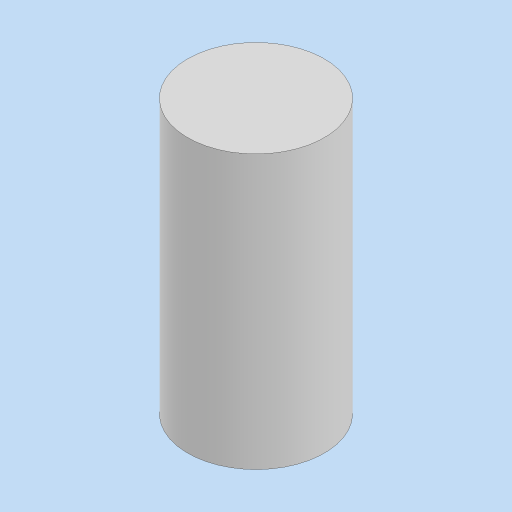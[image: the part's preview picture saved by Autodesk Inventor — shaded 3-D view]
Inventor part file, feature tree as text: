
AUTODESK INVENTOR PART (.ipt)
format: ipt  version: 2024 (Build 280153000, 153)  size: 78,848 bytes
history: native  units: in
note: dims shown in document units (in); Inventor stores cm internally (conversion verified against a paired STEP export)
features: extrude x1, sketch x1
ambient origin geometry x8: Origin, YZ Plane, XZ Plane, XY Plane, X Axis, Y Axis, Z Axis, Center Point
bodies: Solid1 (feature_tree)
feature tree (2):
  extrude  "Extrusion1"  Depth=1.0in TaperAngle=0.0deg
  sketch  "Sketch1"  dims[d0=0.5in d1=1.0in d2=0.0in]
